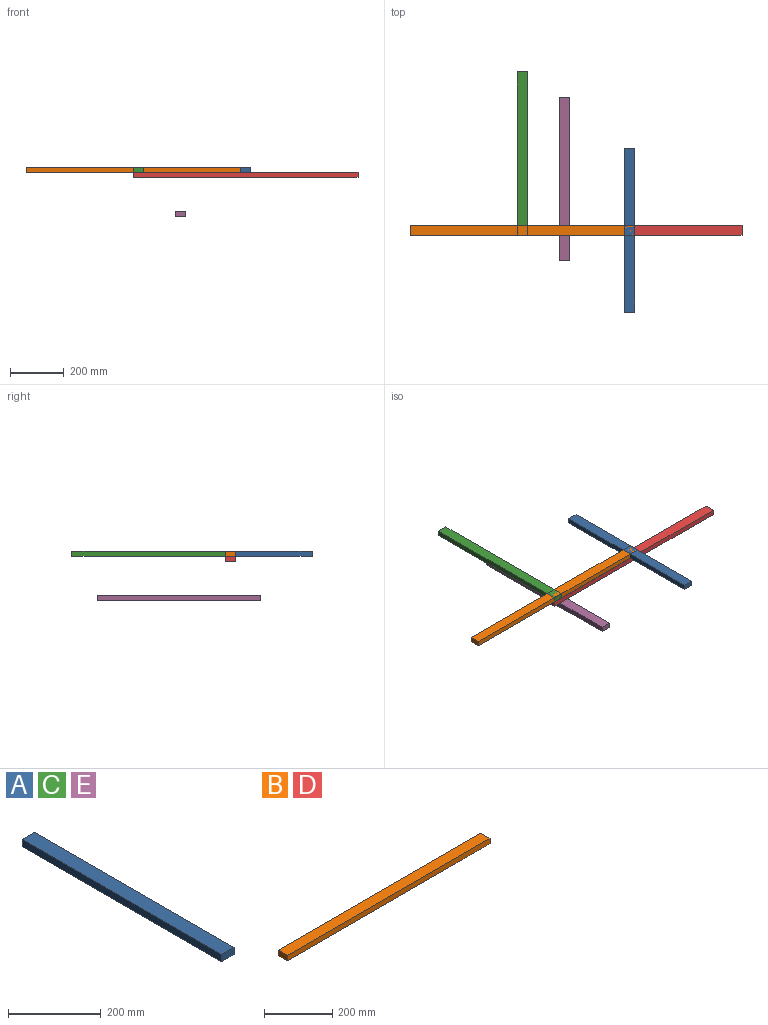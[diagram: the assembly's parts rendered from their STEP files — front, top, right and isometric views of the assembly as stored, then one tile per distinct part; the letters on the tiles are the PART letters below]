
ASSEMBLY  parts=5 mates=5
PART A: 6 faces, bbox 38.1x609.6x19.1 mm
  f0: plane 609.6x19.05mm, normal (-1,0,0), area 11612.9mm2, adj f1,f3,f4,f5
  f1: plane 38.1x19.05mm, normal (0,-1,0), area 725.8mm2, adj f0,f2,f4,f5
  f2: plane 609.6x19.05mm, normal (1,0,0), area 11612.9mm2, adj f1,f3,f4,f5
  f3: plane 38.1x19.05mm, normal (0,1,0), area 725.8mm2, adj f0,f2,f4,f5
  f4: plane 609.6x38.1mm, normal (0,0,1), area 23225.8mm2, adj f0,f1,f2,f3
  f5: plane 609.6x38.1mm, normal (0,0,-1), area 23225.8mm2, adj f0,f1,f2,f3
PART B: 6 faces, bbox 838.2x38.1x19.1 mm
  f0: plane 38.1x19.05mm, normal (-1,0,0), area 725.8mm2, adj f1,f3,f4,f5
  f1: plane 838.2x19.05mm, normal (0,-1,0), area 15967.7mm2, adj f0,f2,f4,f5
  f2: plane 38.1x19.05mm, normal (1,0,0), area 725.8mm2, adj f1,f3,f4,f5
  f3: plane 838.2x19.05mm, normal (0,1,0), area 15967.7mm2, adj f0,f2,f4,f5
  f4: plane 838.2x38.1mm, normal (0,0,1), area 31935.4mm2, adj f0,f1,f2,f3
  f5: plane 838.2x38.1mm, normal (0,0,-1), area 31935.4mm2, adj f0,f1,f2,f3
PART C: same geometry as A
PART D: same geometry as B
PART E: same geometry as A
PLACE A t=(893.26,-132.17,122.27)mm
PLACE B t=(93.16,153.58,122.27)mm
PLACE C t=(493.21,153.58,122.27)mm
PLACE D t=(493.21,153.58,103.22)mm
PLACE E t=(650.89,59.04,-43.96)mm
MATE fastened A.f2 <-> D.f2  axis (1,0,0) through (931.36,172.63,131.8)mm
MATE fastened D.f4 <-> A.f5  axis (0,0,1) through (912.31,172.63,122.27)mm
MATE planar C.f1 <-> D.f1  axis (0,-1,0) through (512.26,153.58,131.8)mm
MATE planar D.f4 <-> C.f5  axis (0,0,1) through (912.31,172.63,122.27)mm
MATE planar D.f0 <-> C.f0  axis (-1,0,0) through (493.21,172.63,112.75)mm
